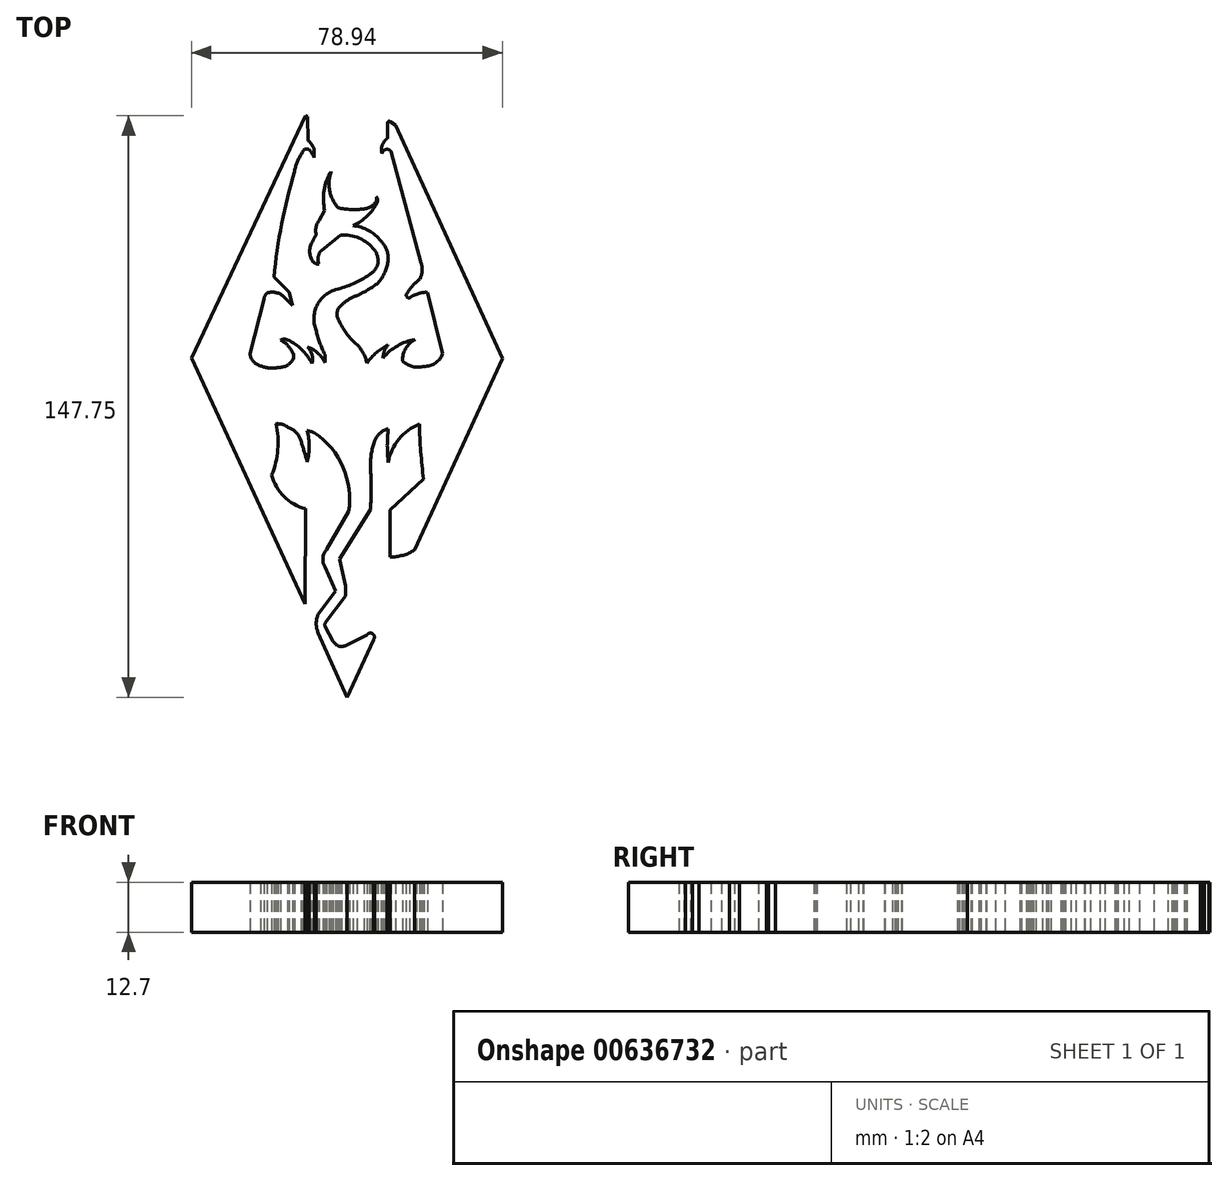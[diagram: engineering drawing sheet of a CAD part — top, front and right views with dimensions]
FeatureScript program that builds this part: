
annotation { "Feature Type Name" : "Feature", "Feature Type Description" : "" }
export const myFeature = defineFeature(function(context is Context, id is Id, definition is map)
    precondition{}
    {
        {
            var Q0;
            Q0=qCreatedBy(makeId("Top.planeOp"),FACE);
            var sketch = newSketch(context, id + "F0", { "sketchPlane" : qUnion([Q0])});
            skLineSegment(sketch, "E0", {"start": v(2.31, 70.96) * mm, "end": v(3.66, 70.03) * mm});
            skLineSegment(sketch, "E1", {"start": v(3.66, 70.03) * mm, "end": v(30.82, 10.8) * mm});
            skLineSegment(sketch, "E2", {"start": v(30.82, 10.8) * mm, "end": v(8.53, -37.92) * mm});
            skLineSegment(sketch, "E3", {"start": v(2.31, -27.7) * mm, "end": v(2.31, -39.7) * mm});
            skLineSegment(sketch, "E4", {"start": v(2.31, -39.7) * mm, "end": v(2.31, -27.7) * mm});
            skLineSegment(sketch, "E5", {"start": v(2.31, -27.7) * mm, "end": v(10.83, -19.92) * mm});
            skArc(sketch, "E6", {"start": v(2.31, -39.7) * mm, "mid": v(5.54, -39.25) * mm, "end": v(8.53, -37.92) * mm});
            skArc(sketch, "E7", {"start": v(9.74, -5.9) * mm, "mid": v(10.1, -12.92) * mm, "end": v(10.83, -19.92) * mm});
            skArc(sketch, "E8", {"start": v(9.74, -5.9) * mm, "mid": v(4.53, -9.73) * mm, "end": v(1.84, -15.62) * mm});
            skArc(sketch, "E9", {"start": v(1.84, -7.1) * mm, "mid": v(1.6, -11.36) * mm, "end": v(1.84, -15.62) * mm});
            skArc(sketch, "E10", {"start": v(1.84, -7.1) * mm, "mid": v(-0.29, -8.26) * mm, "end": v(-1.66, -10.26) * mm});
            skArc(sketch, "E11", {"start": v(-1.66, -10.26) * mm, "mid": v(-2.46, -13.52) * mm, "end": v(-2.7, -16.87) * mm});
            skArc(sketch, "E12", {"start": v(-2.7, -27.54) * mm, "mid": v(-2.48, -22.2) * mm, "end": v(-2.7, -16.87) * mm});
            skLineSegment(sketch, "E13", {"start": v(-2.7, -27.54) * mm, "end": v(-10.53, -40.14) * mm});
            skLineSegment(sketch, "E14", {"start": v(-10.53, -40.14) * mm, "end": v(-8.97, -47) * mm});
            skLineSegment(sketch, "E15", {"start": v(-8.97, -47) * mm, "end": v(-8.97, -49.53) * mm});
            skLineSegment(sketch, "E16", {"start": v(-8.97, -49.53) * mm, "end": v(-14.15, -56.47) * mm});
            skArc(sketch, "E17", {"start": v(-14.15, -56.47) * mm, "mid": v(-14.29, -56.88) * mm, "end": v(-14.15, -57.28) * mm});
            skLineSegment(sketch, "E18", {"start": v(-14.15, -57.28) * mm, "end": v(-12.11, -61.11) * mm});
            skArc(sketch, "E19", {"start": v(-12.11, -61.11) * mm, "mid": v(-10.74, -62.29) * mm, "end": v(-8.93, -62.15) * mm});
            skLineSegment(sketch, "E20", {"start": v(-8.93, -62.15) * mm, "end": v(-3.56, -59.46) * mm});
            skArc(sketch, "E21", {"start": v(-1.93, -60.7) * mm, "mid": v(-2.09, -59.22) * mm, "end": v(-3.56, -59.46) * mm});
            skLineSegment(sketch, "E22", {"start": v(-1.93, -60.7) * mm, "end": v(-8.6, -75.3) * mm});
            skLineSegment(sketch, "E23", {"start": v(-8.6, -75.3) * mm, "end": v(-15.95, -58.93) * mm});
            skArc(sketch, "E24", {"start": v(-15.95, -54.23) * mm, "mid": v(-16.45, -56.58) * mm, "end": v(-15.95, -58.93) * mm});
            skLineSegment(sketch, "E25", {"start": v(-15.95, -54.23) * mm, "end": v(-11.5, -48.26) * mm});
            skLineSegment(sketch, "E26", {"start": v(-11.5, -48.26) * mm, "end": v(-14.15, -42.26) * mm});
            skArc(sketch, "E27", {"start": v(-13.8, -37.77) * mm, "mid": v(-14.76, -39.96) * mm, "end": v(-14.15, -42.26) * mm});
            skLineSegment(sketch, "E28", {"start": v(-13.8, -37.77) * mm, "end": v(-8.22, -28.14) * mm});
            skArc(sketch, "E29", {"start": v(-8.22, -28.14) * mm, "mid": v(-9.64, -16.88) * mm, "end": v(-16.86, -8.13) * mm});
            skArc(sketch, "E30", {"start": v(-16.86, -8.13) * mm, "mid": v(-17.78, -7.8) * mm, "end": v(-18.73, -7.56) * mm});
            skArc(sketch, "E31", {"start": v(-18.73, -15.51) * mm, "mid": v(-18.22, -11.54) * mm, "end": v(-18.73, -7.56) * mm});
            skArc(sketch, "E32", {"start": v(-18.73, -15.51) * mm, "mid": v(-19.52, -12.83) * mm, "end": v(-20.33, -10.15) * mm});
            skArc(sketch, "E33", {"start": v(-20.33, -10.15) * mm, "mid": v(-21.51, -8.05) * mm, "end": v(-23.56, -6.77) * mm});
            skArc(sketch, "E34", {"start": v(-23.56, -6.77) * mm, "mid": v(-25.03, -6) * mm, "end": v(-26.68, -5.83) * mm});
            skArc(sketch, "E35", {"start": v(-27.76, -18.83) * mm, "mid": v(-26.23, -12.41) * mm, "end": v(-26.68, -5.83) * mm});
            skArc(sketch, "E36", {"start": v(-27.76, -18.83) * mm, "mid": v(-24.65, -24.33) * mm, "end": v(-19.12, -27.4) * mm});
            skLineSegment(sketch, "E37", {"start": v(-19.3, -51.63) * mm, "end": v(-19.12, -27.4) * mm});
            skLineSegment(sketch, "E38", {"start": v(-48.12, 10.82) * mm, "end": v(-19.3, -51.63) * mm});
            skLineSegment(sketch, "E39", {"start": v(-48.12, 10.82) * mm, "end": v(-19.12, 72.45) * mm});
            skLineSegment(sketch, "E40", {"start": v(-19.12, 72.45) * mm, "end": v(-18.68, 72.25) * mm});
            skLineSegment(sketch, "E41", {"start": v(-18.68, 72.25) * mm, "end": v(-18.47, 66.17) * mm});
            skArc(sketch, "E42", {"start": v(-16.97, 64.12) * mm, "mid": v(-17.68, 65.17) * mm, "end": v(-18.47, 66.17) * mm});
            skLineSegment(sketch, "E43", {"start": v(-16.97, 64.12) * mm, "end": v(-16.97, 61.85) * mm});
            skArc(sketch, "E44", {"start": v(-16.97, 61.85) * mm, "mid": v(-17.45, 62.74) * mm, "end": v(-18.03, 63.56) * mm});
            skArc(sketch, "E45", {"start": v(-18.03, 63.56) * mm, "mid": v(-18.39, 63.88) * mm, "end": v(-18.84, 64) * mm});
            skArc(sketch, "E46", {"start": v(-18.84, 64) * mm, "mid": v(-19.49, 63.87) * mm, "end": v(-19.86, 63.33) * mm});
            skArc(sketch, "E47", {"start": v(-19.86, 63.33) * mm, "mid": v(-21.18, 60.91) * mm, "end": v(-21.97, 58.27) * mm});
            skArc(sketch, "E48", {"start": v(-21.97, 58.27) * mm, "mid": v(-25.21, 44.96) * mm, "end": v(-27.23, 31.41) * mm});
            skLineSegment(sketch, "E49", {"start": v(-27.23, 31.41) * mm, "end": v(-23.33, 27.6) * mm});
            skLineSegment(sketch, "E50", {"start": v(-23.33, 27.6) * mm, "end": v(-22.51, 24.18) * mm});
            skLineSegment(sketch, "E51", {"start": v(-22.51, 24.18) * mm, "end": v(-24.61, 26.36) * mm});
            skArc(sketch, "E52", {"start": v(-24.61, 26.36) * mm, "mid": v(-26.62, 27.51) * mm, "end": v(-28.93, 27.41) * mm});
            skArc(sketch, "E53", {"start": v(-28.93, 27.41) * mm, "mid": v(-29.49, 26.7) * mm, "end": v(-29.71, 25.82) * mm});
            skLineSegment(sketch, "E54", {"start": v(-29.71, 25.82) * mm, "end": v(-33.25, 11.96) * mm});
            skArc(sketch, "E55", {"start": v(-33.25, 11.96) * mm, "mid": v(-32.43, 10.02) * mm, "end": v(-30.65, 8.9) * mm});
            skArc(sketch, "E56", {"start": v(-30.65, 8.9) * mm, "mid": v(-28.4, 8.33) * mm, "end": v(-26.1, 8.46) * mm});
            skArc(sketch, "E57", {"start": v(-26.1, 8.46) * mm, "mid": v(-23.9, 9) * mm, "end": v(-22.28, 10.58) * mm});
            skArc(sketch, "E58", {"start": v(-22.28, 10.58) * mm, "mid": v(-22.2, 11.3) * mm, "end": v(-22.28, 12.04) * mm});
            skArc(sketch, "E59", {"start": v(-22.28, 12.04) * mm, "mid": v(-23.63, 14) * mm, "end": v(-25.45, 15.51) * mm});
            skArc(sketch, "E60", {"start": v(-23.7, 15.51) * mm, "mid": v(-24.58, 15.67) * mm, "end": v(-25.45, 15.51) * mm});
            skArc(sketch, "E61", {"start": v(-17.56, 9.49) * mm, "mid": v(-20.12, 13.02) * mm, "end": v(-23.7, 15.51) * mm});
            skArc(sketch, "E62", {"start": v(-17.56, 9.49) * mm, "mid": v(-17.52, 11.77) * mm, "end": v(-18.71, 13.72) * mm});
            skArc(sketch, "E63", {"start": v(-14.25, 9.78) * mm, "mid": v(-16.09, 12.2) * mm, "end": v(-18.71, 13.72) * mm});
            skArc(sketch, "E64", {"start": v(-14.25, 9.78) * mm, "mid": v(-14.17, 10.78) * mm, "end": v(-14.25, 11.78) * mm});
            skArc(sketch, "E65", {"start": v(-16.52, 18.02) * mm, "mid": v(-15.58, 14.83) * mm, "end": v(-14.25, 11.78) * mm});
            skArc(sketch, "E66", {"start": v(-16.1, 24.6) * mm, "mid": v(-17.03, 21.35) * mm, "end": v(-16.52, 18.02) * mm});
            skArc(sketch, "E67", {"start": v(-11.49, 28.25) * mm, "mid": v(-14.15, 26.87) * mm, "end": v(-16.1, 24.6) * mm});
            skArc(sketch, "E68", {"start": v(-11.49, 28.25) * mm, "mid": v(-7.03, 29.79) * mm, "end": v(-2.9, 32.06) * mm});
            skArc(sketch, "E69", {"start": v(-2.9, 32.06) * mm, "mid": v(-1.65, 33.2) * mm, "end": v(-0.83, 34.67) * mm});
            skArc(sketch, "E70", {"start": v(-0.83, 34.67) * mm, "mid": v(-0.87, 36.6) * mm, "end": v(-1.68, 38.36) * mm});
            skArc(sketch, "E71", {"start": v(-1.68, 38.36) * mm, "mid": v(-5.53, 41.33) * mm, "end": v(-10.32, 42.1) * mm});
            skLineSegment(sketch, "E72", {"start": v(-10.32, 42.1) * mm, "end": v(-15.1, 38.24) * mm});
            skArc(sketch, "E73", {"start": v(-15.1, 38.24) * mm, "mid": v(-15.51, 37.78) * mm, "end": v(-15.73, 37.2) * mm});
            skArc(sketch, "E74", {"start": v(-15.73, 37.2) * mm, "mid": v(-16.02, 35.97) * mm, "end": v(-15.73, 34.74) * mm});
            skArc(sketch, "E75", {"start": v(-17.23, 35.3) * mm, "mid": v(-16.54, 34.86) * mm, "end": v(-15.73, 34.74) * mm});
            skArc(sketch, "E76", {"start": v(-17.23, 40.74) * mm, "mid": v(-18.12, 38.02) * mm, "end": v(-17.23, 35.3) * mm});
            skArc(sketch, "E77", {"start": v(-16.45, 42.15) * mm, "mid": v(-16.9, 41.48) * mm, "end": v(-17.23, 40.74) * mm});
            skArc(sketch, "E78", {"start": v(-15.73, 45.83) * mm, "mid": v(-16.5, 44.07) * mm, "end": v(-16.45, 42.15) * mm});
            skLineSegment(sketch, "E79", {"start": v(-15.73, 45.83) * mm, "end": v(-14.27, 48.33) * mm});
            skArc(sketch, "E80", {"start": v(-12.66, 58.24) * mm, "mid": v(-14.48, 53.45) * mm, "end": v(-14.27, 48.33) * mm});
            skArc(sketch, "E81", {"start": v(-12.66, 58.24) * mm, "mid": v(-13.1, 56.45) * mm, "end": v(-13.2, 54.6) * mm});
            skArc(sketch, "E82", {"start": v(-13.2, 54.6) * mm, "mid": v(-12.5, 51.64) * mm, "end": v(-10.9, 49.05) * mm});
            skArc(sketch, "E83", {"start": v(-10.9, 49.05) * mm, "mid": v(-7.62, 48.61) * mm, "end": v(-4.32, 48.75) * mm});
            skArc(sketch, "E84", {"start": v(-4.32, 48.75) * mm, "mid": v(-2.57, 49.38) * mm, "end": v(-1.21, 50.64) * mm});
            skArc(sketch, "E85", {"start": v(-1.21, 50.64) * mm, "mid": v(-1.1, 51.25) * mm, "end": v(-1.21, 51.85) * mm});
            skArc(sketch, "E86", {"start": v(-0.86, 50.64) * mm, "mid": v(-0.88, 51.3) * mm, "end": v(-1.21, 51.85) * mm});
            skArc(sketch, "E87", {"start": v(-7.13, 44.5) * mm, "mid": v(-3.44, 47.01) * mm, "end": v(-0.86, 50.64) * mm});
            skArc(sketch, "E88", {"start": v(0, 40.63) * mm, "mid": v(-3.16, 43.31) * mm, "end": v(-7.13, 44.5) * mm});
            skArc(sketch, "E89", {"start": v(1.8, 35.79) * mm, "mid": v(1.4, 38.4) * mm, "end": v(0, 40.63) * mm});
            skArc(sketch, "E90", {"start": v(-0.75, 29.96) * mm, "mid": v(1, 32.67) * mm, "end": v(1.8, 35.79) * mm});
            skArc(sketch, "E91", {"start": v(-6.05, 26.76) * mm, "mid": v(-3.32, 28.22) * mm, "end": v(-0.75, 29.96) * mm});
            skArc(sketch, "E92", {"start": v(-6.05, 26.76) * mm, "mid": v(-8.17, 25.8) * mm, "end": v(-9.98, 24.34) * mm});
            skArc(sketch, "E93", {"start": v(-9.98, 24.34) * mm, "mid": v(-11.14, 22.52) * mm, "end": v(-10.7, 20.4) * mm});
            skArc(sketch, "E94", {"start": v(-10.7, 20.4) * mm, "mid": v(-8.74, 17.06) * mm, "end": v(-6.05, 14.26) * mm});
            skArc(sketch, "E95", {"start": v(-3.56, 9.61) * mm, "mid": v(-4.5, 12.1) * mm, "end": v(-6.05, 14.26) * mm});
            skArc(sketch, "E96", {"start": v(1.8, 14.26) * mm, "mid": v(-1.16, 12.26) * mm, "end": v(-3.56, 9.61) * mm});
            skArc(sketch, "E97", {"start": v(1.8, 14.26) * mm, "mid": v(0.87, 12.7) * mm, "end": v(0.56, 10.93) * mm});
            skArc(sketch, "E98", {"start": v(8.6, 15.57) * mm, "mid": v(4.16, 13.99) * mm, "end": v(0.56, 10.93) * mm});
            skArc(sketch, "E99", {"start": v(8.6, 15.57) * mm, "mid": v(6.24, 13.3) * mm, "end": v(5.5, 10.1) * mm});
            skArc(sketch, "E100", {"start": v(5.5, 10.1) * mm, "mid": v(8.02, 8.72) * mm, "end": v(10.9, 8.76) * mm});
            skArc(sketch, "E101", {"start": v(10.9, 8.76) * mm, "mid": v(13.83, 9.6) * mm, "end": v(15.67, 12.03) * mm});
            skLineSegment(sketch, "E102", {"start": v(15.67, 12.03) * mm, "end": v(11.76, 27.55) * mm});
            skArc(sketch, "E103", {"start": v(11.76, 27.55) * mm, "mid": v(10.34, 27.48) * mm, "end": v(9, 27) * mm});
            skArc(sketch, "E104", {"start": v(9, 27) * mm, "mid": v(8.1, 26.72) * mm, "end": v(7.3, 26.18) * mm});
            skArc(sketch, "E105", {"start": v(6.42, 27) * mm, "mid": v(6.64, 26.35) * mm, "end": v(7.3, 26.18) * mm});
            skArc(sketch, "E106", {"start": v(9.9, 30.96) * mm, "mid": v(7.96, 29.16) * mm, "end": v(6.42, 27) * mm});
            skArc(sketch, "E107", {"start": v(9.9, 30.96) * mm, "mid": v(10.43, 32.93) * mm, "end": v(10.22, 34.97) * mm});
            skLineSegment(sketch, "E108", {"start": v(2.54, 63.37) * mm, "end": v(10.22, 34.97) * mm});
            skArc(sketch, "E109", {"start": v(1.64, 66.65) * mm, "mid": v(1.23, 66.4) * mm, "end": v(0.96, 66) * mm});
            skLineSegment(sketch, "E110", {"start": v(1.64, 66.65) * mm, "end": v(1.64, 70.6) * mm});
            skArc(sketch, "E111", {"start": v(2.31, 70.96) * mm, "mid": v(1.87, 70.97) * mm, "end": v(1.64, 70.6) * mm});
            skPoint(sketch, "E112.endSnap0", {"position": v(7.7, 48.8) * mm});
            skArc(sketch, "E113", {"start": v(2.54, 63.37) * mm, "mid": v(1.2, 63.87) * mm, "end": v(0.29, 62.76) * mm});
            skArc(sketch, "E114", {"start": v(0.96, 66) * mm, "mid": v(0.19, 64.47) * mm, "end": v(0.29, 62.76) * mm});
            skSolve(sketch);
        }
        {
            var Q0;
            Q0 = qSketchRegion(id + "F0", true);
            extrude(context, id + "F1", {"entities" : qUnion([Q0]), "depth" : 12.7 * mm, "offsetDistance" : 25.4 * mm});
        }
    });
